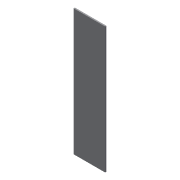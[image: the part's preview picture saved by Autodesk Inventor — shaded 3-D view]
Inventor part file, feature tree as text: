
AUTODESK INVENTOR PART (.ipt)
format: ipt  version: 2018 (Build 220112000, 112)  size: 123,392 bytes
history: native  units: in
note: dims shown in document units (in); Inventor stores cm internally (conversion verified against a paired STEP export)
features: reference x6, sketch x4, other x4, hole x2, extrude x1
ambient origin geometry x8: Origin, YZ Plane, XZ Plane, XY Plane, X Axis, Y Axis, Z Axis, Center Point
bodies: Solid1 (feature_tree)
feature tree (17):
  extrude  "Extrusion1"  Depth=2.25in
  sketch  "Sketch2"  dims[d2=0.125in d3=0.0in]
  hole  "Hole1"  [1 undecoded]
  hole  "Hole2"  [1 undecoded]
  sketch  "Sketch1"  dims[d0=12.0in d1=2.25in]
  reference  "Reference1"
  reference  "Reference2"
  reference  "Reference3"
  reference  "Reference4"
  reference  "Reference5"
  reference  "Reference6"
  sketch  "Sketch3"  dims[d4=0.177in d5=0.75in d6=0.332in d7=0.25in d8=0.5635in d9=1.0in d10=0.8108in d11=0.375in]
  sketch  "Sketch4"  dims[d12=0.375in d13=0.375in d14=0.375in d15=0.5in d16=0.5in d17=4.7244in d19=1.0in d20=0.3937in d22=1.0in d24=0.177in d25=0.75in d26=0.332in d27=0.25in d28=0.5635in d29=1.0in d30=0.8108in]
  parser-record x1  (decoder bookkeeping rows leaked as tree rows — omitted from the tree; the rows remain in map.json)
  other  "Glyf bot.iam"
  other  "Clampy arm:2"
  other  "Clampy arm:1"
note: 2 required parameter values undecoded (feature->parameter linkage not recoverable at this tier; creation-order binding heuristic only, values carry confidence <= 0.55)
note: 1 file-system path scrubbed to <path> (originals preserved in map.json)
